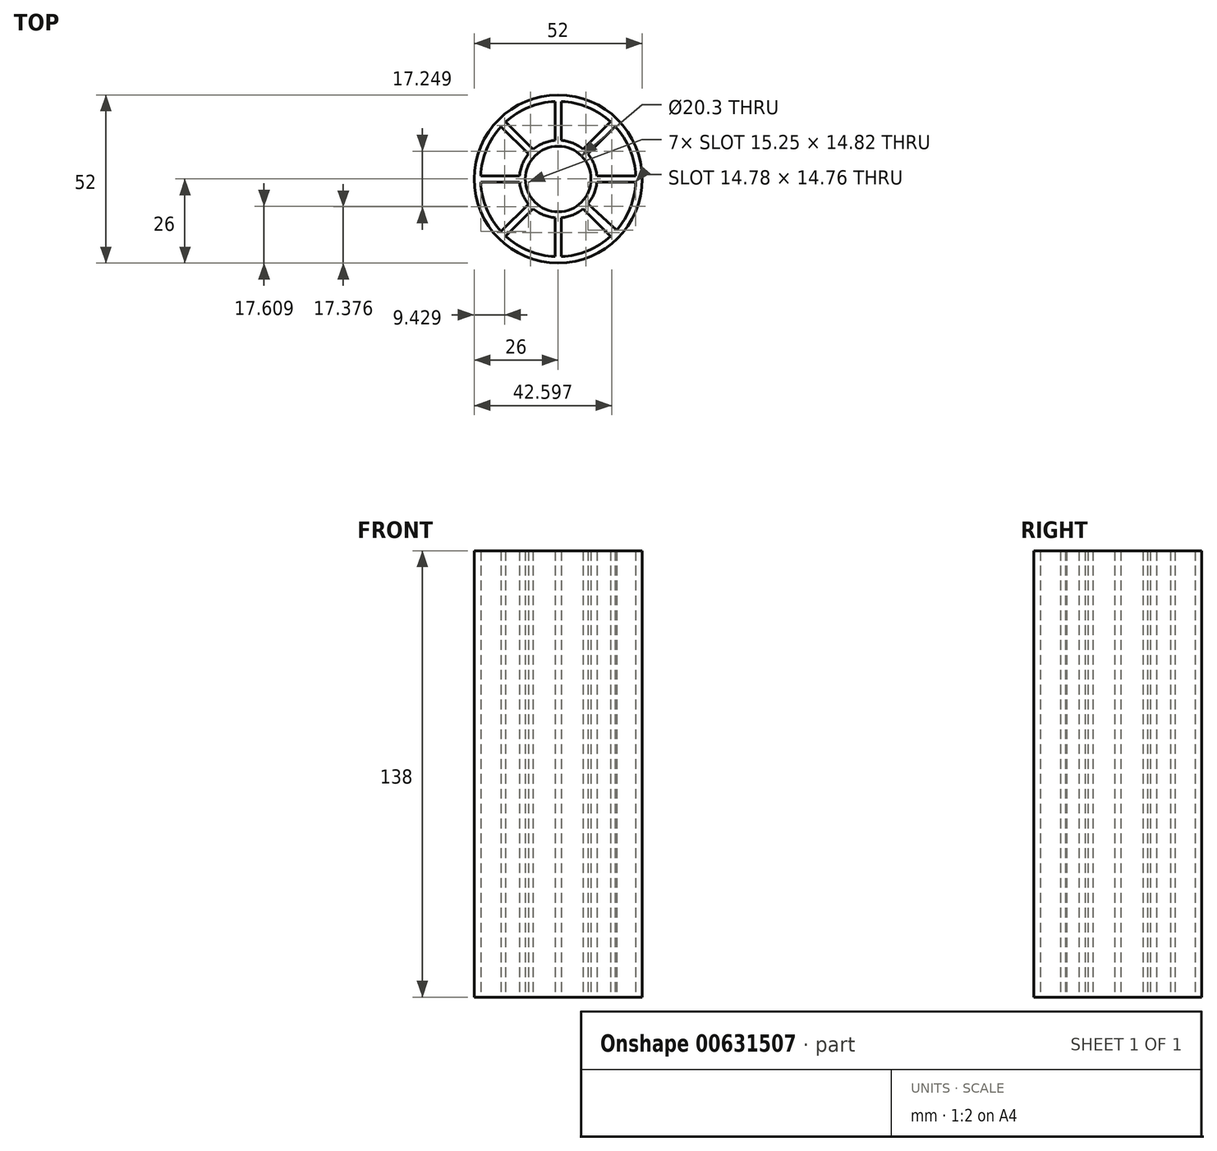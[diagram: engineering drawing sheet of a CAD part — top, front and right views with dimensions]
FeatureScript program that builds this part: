
annotation { "Feature Type Name" : "Feature", "Feature Type Description" : "" }
export const myFeature = defineFeature(function(context is Context, id is Id, definition is map)
    precondition{}
    {
        {
            var Q0;
            Q0=qCreatedBy(makeId("Top.planeOp"),FACE);
            var sketch = newSketch(context, id + "F0", { "sketchPlane" : qUnion([Q0])});
            skCircle(sketch, "E0", {"center": v(0, 0) * mm, "radius": 26 * mm});
            skArc(sketch, "E1", {"start": v(-7.18, 7.18) * mm, "mid": v(-10.15, 0) * mm, "end": v(-7.18, -7.18) * mm});
            skArc(sketch, "E2", {"start": v(-2.97, 9.7) * mm, "mid": v(-5.23, 8.7) * mm, "end": v(-7.18, 7.18) * mm});
            skArc(sketch, "E3", {"start": v(-7.18, -7.18) * mm, "mid": v(9.38, -3.88) * mm, "end": v(0, 10.15) * mm});
            skLineSegment(sketch, "E4", {"start": v(-7.18, -7.18) * mm, "end": v(-7.18, -7.18) * mm});
            skArc(sketch, "E5", {"start": v(0, 10.15) * mm, "mid": v(-1.5, 10.04) * mm, "end": v(-2.97, 9.7) * mm});
            skLineSegment(sketch, "E6.6.1", {"start": v(7.75, -9.16) * mm, "end": v(16.25, -17.66) * mm});
            skLineSegment(sketch, "E6.7.1", {"start": v(11.96, -1) * mm, "end": v(23.98, -1) * mm});
            skCircle(sketch, "E7", {"center": v(0, 0) * mm, "radius": 12 * mm});
            skCircle(sketch, "E8", {"center": v(0, 0) * mm, "radius": 24 * mm});
            skLineSegment(sketch, "E9", {"start": v(-9.16, 7.75) * mm, "end": v(-17.66, 16.25) * mm});
            skLineSegment(sketch, "E10", {"start": v(-7.75, 9.16) * mm, "end": v(-16.25, 17.66) * mm});
            skLineSegment(sketch, "E11", {"start": v(-1, 11.96) * mm, "end": v(-1, 23.98) * mm});
            skLineSegment(sketch, "E12", {"start": v(1, 11.96) * mm, "end": v(1, 23.98) * mm});
            skLineSegment(sketch, "E13", {"start": v(7.75, 9.16) * mm, "end": v(16.25, 17.66) * mm});
            skLineSegment(sketch, "E14", {"start": v(9.16, 7.75) * mm, "end": v(17.66, 16.25) * mm});
            skLineSegment(sketch, "E15", {"start": v(11.96, 1) * mm, "end": v(23.98, 1) * mm});
            skLineSegment(sketch, "E16", {"start": v(9.22, -7.69) * mm, "end": v(18.08, -15.78) * mm});
            skLineSegment(sketch, "E17", {"start": v(1, -11.96) * mm, "end": v(1, -23.98) * mm});
            skLineSegment(sketch, "E18", {"start": v(-1, -11.96) * mm, "end": v(-1, -23.98) * mm});
            skLineSegment(sketch, "E19", {"start": v(-7.75, -9.16) * mm, "end": v(-16.25, -17.66) * mm});
            skLineSegment(sketch, "E20", {"start": v(-9.16, -7.75) * mm, "end": v(-17.66, -16.25) * mm});
            skLineSegment(sketch, "E21", {"start": v(-11.96, -1) * mm, "end": v(-23.98, -1) * mm});
            skLineSegment(sketch, "E22", {"start": v(-11.96, 1) * mm, "end": v(-23.98, 1) * mm});
            skLineSegment(sketch, "E23", {"start": v(16.7, -17.23) * mm, "end": v(16.7, -17.23) * mm});
            skLineSegment(sketch, "E24", {"start": v(16.67, -17.2) * mm, "end": v(16.7, -17.23) * mm});
            skSolve(sketch);
        }
        {
            var Q0;
            Q0 = qSketchRegion(id + "F0", true);
            var Q1;
            {var subQ0=sQuery(id+"F0.wireOp",EDGE,"E19");Q1=makeQuery(id+"F0.imprint","IMPRINT",FACE,{"disambiguationData":[TD([[makeQuery(id+"F0.imprint","IMPRINT",EDGE,{"derivedFrom":subQ0}),-1.0]])]});}
            var Q2;
            Q2=makeQuery(id+"F0.imprint","IMPRINT",FACE,{"disambiguationData":[TD([[makeQuery(id+"F0.imprint","IMPRINT",EDGE,{"derivedFrom":sQuery(id+"F0.wireOp",EDGE,"E1")}),-1.0]])]});
            var Q3;
            {var subQ0=sQuery(id+"F0.wireOp",EDGE,"E17");Q3=makeQuery(id+"F0.imprint","IMPRINT",FACE,{"disambiguationData":[TD([[makeQuery(id+"F0.imprint","IMPRINT",EDGE,{"derivedFrom":subQ0}),-1.0]])]});}
            var Q4;
            {var subQ4=sQuery(id+"F0.wireOp",EDGE,"E6.6.1");Q4=makeQuery(id+"F0.imprint","IMPRINT",FACE,{"disambiguationData":[TD([[makeQuery(id+"F0.imprint","IMPRINT",EDGE,{"derivedFrom":subQ4}),1.0]])]});}
            var Q5;
            {var subQ0=sQuery(id+"F0.wireOp",EDGE,"E15");Q5=makeQuery(id+"F0.imprint","IMPRINT",FACE,{"disambiguationData":[TD([[makeQuery(id+"F0.imprint","IMPRINT",EDGE,{"derivedFrom":subQ0}),-1.0]])]});}
            var Q6;
            {var subQ0=sQuery(id+"F0.wireOp",EDGE,"E13");Q6=makeQuery(id+"F0.imprint","IMPRINT",FACE,{"disambiguationData":[TD([[makeQuery(id+"F0.imprint","IMPRINT",EDGE,{"derivedFrom":subQ0}),-1.0]])]});}
            var Q7;
            {var subQ0=sQuery(id+"F0.wireOp",EDGE,"E11");Q7=makeQuery(id+"F0.imprint","IMPRINT",FACE,{"disambiguationData":[TD([[makeQuery(id+"F0.imprint","IMPRINT",EDGE,{"derivedFrom":subQ0}),-1.0]])]});}
            var Q8;
            {var subQ0=sQuery(id+"F0.wireOp",EDGE,"E9");Q8=makeQuery(id+"F0.imprint","IMPRINT",FACE,{"disambiguationData":[TD([[makeQuery(id+"F0.imprint","IMPRINT",EDGE,{"derivedFrom":subQ0}),-1.0]])]});}
            var Q9;
            {var subQ0=sQuery(id+"F0.wireOp",EDGE,"E21");Q9=makeQuery(id+"F0.imprint","IMPRINT",FACE,{"disambiguationData":[TD([[makeQuery(id+"F0.imprint","IMPRINT",EDGE,{"derivedFrom":subQ0}),-1.0]])]});}
            extrude(context, id + "F1", {"entities" : qUnion([Q0, Q1, Q2, Q3, Q4, Q5, Q6, Q7, Q8, Q9]), "depth" : 138 * mm, "offsetDistance" : 25 * mm});
        }
    });
